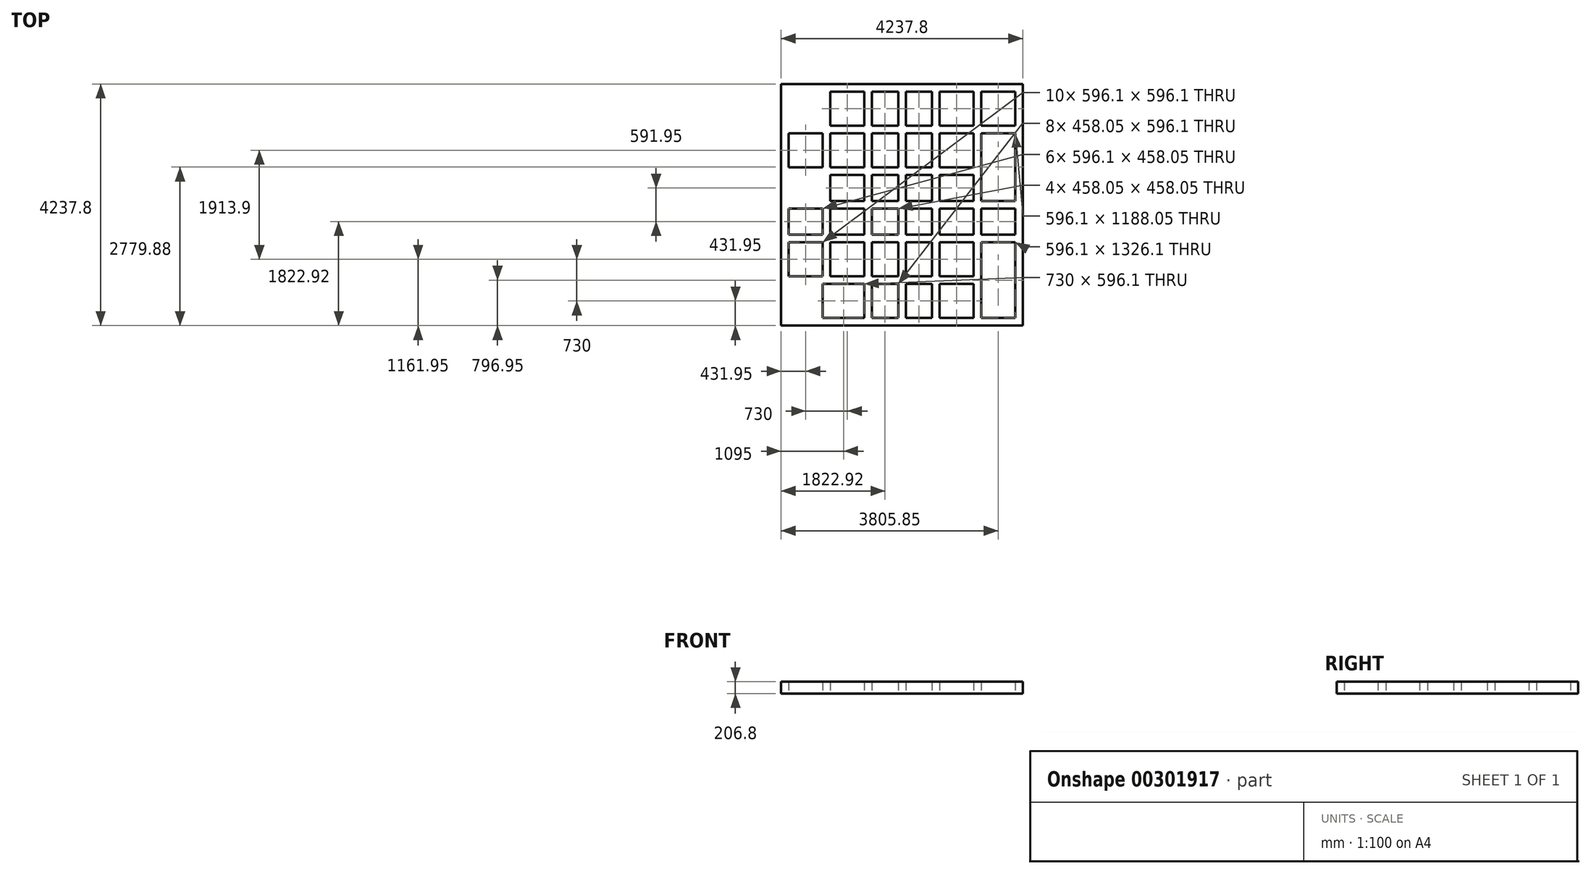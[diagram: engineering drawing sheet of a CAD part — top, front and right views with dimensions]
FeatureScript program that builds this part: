
annotation { "Feature Type Name" : "Feature", "Feature Type Description" : "" }
export const myFeature = defineFeature(function(context is Context, id is Id, definition is map)
    precondition{}
    {
        {
            var Q0;
            Q0=qCreatedBy(makeId("Top.planeOp"),FACE);
            var sketch = newSketch(context, id + "F0", { "sketchPlane" : qUnion([Q0])});
            skCircle(sketch, "E0", {"center": v(0, 0) * mm, "radius": 1985 * mm});
            skLineSegment(sketch, "E1.bottom", {"start": v(-2118.9, 2118.9) * mm, "end": v(2118.9, 2118.9) * mm});
            skLineSegment(sketch, "E1.top", {"start": v(-2118.9, -2118.9) * mm, "end": v(2118.9, -2118.9) * mm});
            skLineSegment(sketch, "E1.left", {"start": v(-2118.9, 2118.9) * mm, "end": v(-2118.9, -2118.9) * mm});
            skLineSegment(sketch, "E1.right", {"start": v(2118.9, 2118.9) * mm, "end": v(2118.9, -2118.9) * mm});
            skLineSegment(sketch, "E2.bottom", {"start": v(-1985, 1985) * mm, "end": v(1985, 1985) * mm});
            skLineSegment(sketch, "E2.top", {"start": v(-1985, -1985) * mm, "end": v(1985, -1985) * mm});
            skLineSegment(sketch, "E2.left", {"start": v(-1985, 1985) * mm, "end": v(-1985, -1985) * mm});
            skLineSegment(sketch, "E2.right", {"start": v(1985, 1985) * mm, "end": v(1985, -1985) * mm});
            skLineSegment(sketch, "E3", {"start": v(1388.9, -1985) * mm, "end": v(1388.9, 1985) * mm});
            skLineSegment(sketch, "E4", {"start": v(1255, -1985) * mm, "end": v(1255, 1985) * mm});
            skLineSegment(sketch, "E5", {"start": v(-525, 1985) * mm, "end": v(-525, -1985) * mm});
            skLineSegment(sketch, "E6", {"start": v(-658.9, 1985) * mm, "end": v(-658.9, -1985) * mm});
            skLineSegment(sketch, "E7", {"start": v(-1255, 1985) * mm, "end": v(-1255, -1985) * mm});
            skLineSegment(sketch, "E8", {"start": v(-1388.9, 1985) * mm, "end": v(-1388.9, -1985) * mm});
            skLineSegment(sketch, "E9", {"start": v(525, 1985) * mm, "end": v(525, -1985) * mm});
            skLineSegment(sketch, "E10", {"start": v(658.9, 1985) * mm, "end": v(658.9, -1985) * mm});
            skLineSegment(sketch, "E11", {"start": v(-1985, 1388.9) * mm, "end": v(1985, 1388.9) * mm});
            skLineSegment(sketch, "E12", {"start": v(-1985, 1255) * mm, "end": v(1985, 1255) * mm});
            skLineSegment(sketch, "E13", {"start": v(-1985, -1388.9) * mm, "end": v(1985, -1388.9) * mm});
            skLineSegment(sketch, "E14", {"start": v(-1985, -1255) * mm, "end": v(1985, -1255) * mm});
            skLineSegment(sketch, "E15", {"start": v(-1985, 658.9) * mm, "end": v(1985, 658.9) * mm});
            skLineSegment(sketch, "E16", {"start": v(-1985, 525) * mm, "end": v(1985, 525) * mm});
            skLineSegment(sketch, "E17", {"start": v(-1985, -525) * mm, "end": v(1985, -525) * mm});
            skLineSegment(sketch, "E18", {"start": v(-1985, -658.9) * mm, "end": v(1985, -658.9) * mm});
            skLineSegment(sketch, "E19", {"start": v(-66.95, 1985) * mm, "end": v(-66.95, -1985) * mm});
            skPoint(sketch, "E19.endSnap0", {"position": v(0, -1985) * mm});
            skLineSegment(sketch, "E20", {"start": v(66.95, 1985) * mm, "end": v(66.95, -1985) * mm});
            skLineSegment(sketch, "E21", {"start": v(-1985, 66.95) * mm, "end": v(1985, 66.95) * mm});
            skLineSegment(sketch, "E22", {"start": v(-1985, -66.95) * mm, "end": v(1985, -66.95) * mm});
            skSolve(sketch);
        }
        {
            var Q0;
            {var subQ0=sQuery(id+"F0.wireOp",EDGE,"E7");var subQ1=sQuery(id+"F0.wireOp",EDGE,"E0");var subQ2=makeQuery(id+"F0.imprint","INTERSECT",VERTEX,{"disambiguationData":[OD(0.0)],"derivedFrom":[subQ1,subQ0]});Q0=makeQuery(id+"F0.imprint","IMPRINT",FACE,{"disambiguationData":[TD([[makeQuery(id+"F0.imprint","IMPRINT",EDGE,{"disambiguationData":[TD([[subQ2,-1.0]])],"derivedFrom":subQ1}),-1.0]])]});}
            var Q1;
            {var subQ0=sQuery(id+"F0.wireOp",EDGE,"E5");var subQ1=sQuery(id+"F0.wireOp",EDGE,"E0");var subQ2=makeQuery(id+"F0.imprint","INTERSECT",VERTEX,{"disambiguationData":[OD(0.0)],"derivedFrom":[subQ1,subQ0]});Q1=makeQuery(id+"F0.imprint","IMPRINT",FACE,{"disambiguationData":[TD([[makeQuery(id+"F0.imprint","IMPRINT",EDGE,{"disambiguationData":[TD([[subQ2,-1.0]])],"derivedFrom":subQ1}),1.0]])]});}
            var Q2;
            {var subQ0=sQuery(id+"F0.wireOp",EDGE,"E5");var subQ1=sQuery(id+"F0.wireOp",EDGE,"E0");var subQ2=makeQuery(id+"F0.imprint","INTERSECT",VERTEX,{"disambiguationData":[OD(0.0)],"derivedFrom":[subQ1,subQ0]});Q2=makeQuery(id+"F0.imprint","IMPRINT",FACE,{"disambiguationData":[TD([[makeQuery(id+"F0.imprint","IMPRINT",EDGE,{"disambiguationData":[TD([[subQ2,-1.0]])],"derivedFrom":subQ1}),-1.0]])]});}
            var Q3;
            Q3=makeQuery(id+"F0.imprint","IMPRINT",FACE,{"disambiguationData":[TD([[makeQuery(id+"F0.imprint","IMPRINT",EDGE,{"derivedFrom":sQuery(id+"F0.wireOp",EDGE,"E1.bottom")}),-1.0]])]});
            var Q4;
            {var subQ0=sQuery(id+"F0.wireOp",EDGE,"E11");var subQ1=sQuery(id+"F0.wireOp",EDGE,"E0");var subQ2=makeQuery(id+"F0.imprint","INTERSECT",VERTEX,{"disambiguationData":[OD(1.0)],"derivedFrom":[subQ1,subQ0]});Q4=makeQuery(id+"F0.imprint","IMPRINT",FACE,{"disambiguationData":[TD([[makeQuery(id+"F0.imprint","IMPRINT",EDGE,{"disambiguationData":[TD([[subQ2,-1.0]])],"derivedFrom":subQ1}),-1.0]])]});}
            var Q5;
            {var subQ0=sQuery(id+"F0.wireOp",EDGE,"E11");var subQ1=sQuery(id+"F0.wireOp",EDGE,"E0");var subQ2=makeQuery(id+"F0.imprint","INTERSECT",VERTEX,{"disambiguationData":[OD(1.0)],"derivedFrom":[subQ1,subQ0]});Q5=makeQuery(id+"F0.imprint","IMPRINT",FACE,{"disambiguationData":[TD([[makeQuery(id+"F0.imprint","IMPRINT",EDGE,{"disambiguationData":[TD([[subQ2,-1.0]])],"derivedFrom":subQ1}),1.0]])]});}
            var Q6;
            {var subQ0=sQuery(id+"F0.wireOp",EDGE,"E11");var subQ1=sQuery(id+"F0.wireOp",EDGE,"E7");var subQ2=makeQuery(id+"F0.imprint","INTERSECT",VERTEX,{"derivedFrom":[subQ1,subQ0]});Q6=makeQuery(id+"F0.imprint","IMPRINT",FACE,{"disambiguationData":[TD([[makeQuery(id+"F0.imprint","IMPRINT",EDGE,{"disambiguationData":[TD([[subQ2,-1.0]])],"derivedFrom":subQ1}),-1.0]])]});}
            var Q7;
            {var subQ0=sQuery(id+"F0.wireOp",EDGE,"E11");var subQ1=sQuery(id+"F0.wireOp",EDGE,"E6");var subQ2=makeQuery(id+"F0.imprint","INTERSECT",VERTEX,{"derivedFrom":[subQ1,subQ0]});Q7=makeQuery(id+"F0.imprint","IMPRINT",FACE,{"disambiguationData":[TD([[makeQuery(id+"F0.imprint","IMPRINT",EDGE,{"disambiguationData":[TD([[subQ2,-1.0]])],"derivedFrom":subQ1}),-1.0]])]});}
            var Q8;
            {var subQ0=sQuery(id+"F0.wireOp",EDGE,"E7");var subQ1=sQuery(id+"F0.wireOp",EDGE,"E0");var subQ2=makeQuery(id+"F0.imprint","INTERSECT",VERTEX,{"disambiguationData":[OD(0.0)],"derivedFrom":[subQ1,subQ0]});Q8=makeQuery(id+"F0.imprint","IMPRINT",FACE,{"disambiguationData":[TD([[makeQuery(id+"F0.imprint","IMPRINT",EDGE,{"disambiguationData":[TD([[subQ2,-1.0]])],"derivedFrom":subQ1}),1.0]])]});}
            var Q9;
            {var subQ0=sQuery(id+"F0.wireOp",EDGE,"E12");var subQ1=sQuery(id+"F0.wireOp",EDGE,"E7");var subQ2=makeQuery(id+"F0.imprint","INTERSECT",VERTEX,{"derivedFrom":[subQ1,subQ0]});Q9=makeQuery(id+"F0.imprint","IMPRINT",FACE,{"disambiguationData":[TD([[makeQuery(id+"F0.imprint","IMPRINT",EDGE,{"disambiguationData":[TD([[subQ2,-1.0]])],"derivedFrom":subQ1}),-1.0]])]});}
            var Q10;
            {var subQ0=sQuery(id+"F0.wireOp",EDGE,"E16");var subQ1=sQuery(id+"F0.wireOp",EDGE,"E7");var subQ2=makeQuery(id+"F0.imprint","INTERSECT",VERTEX,{"derivedFrom":[subQ1,subQ0]});Q10=makeQuery(id+"F0.imprint","IMPRINT",FACE,{"disambiguationData":[TD([[makeQuery(id+"F0.imprint","IMPRINT",EDGE,{"disambiguationData":[TD([[subQ2,-1.0]])],"derivedFrom":subQ1}),-1.0]])]});}
            var Q11;
            {var subQ0=sQuery(id+"F0.wireOp",EDGE,"E15");var subQ1=sQuery(id+"F0.wireOp",EDGE,"E7");var subQ2=makeQuery(id+"F0.imprint","INTERSECT",VERTEX,{"derivedFrom":[subQ1,subQ0]});Q11=makeQuery(id+"F0.imprint","IMPRINT",FACE,{"disambiguationData":[TD([[makeQuery(id+"F0.imprint","IMPRINT",EDGE,{"disambiguationData":[TD([[subQ2,-1.0]])],"derivedFrom":subQ1}),-1.0]])]});}
            var Q12;
            {var subQ0=sQuery(id+"F0.wireOp",EDGE,"E15");var subQ1=sQuery(id+"F0.wireOp",EDGE,"E0");var subQ2=makeQuery(id+"F0.imprint","INTERSECT",VERTEX,{"disambiguationData":[OD(1.0)],"derivedFrom":[subQ1,subQ0]});Q12=makeQuery(id+"F0.imprint","IMPRINT",FACE,{"disambiguationData":[TD([[makeQuery(id+"F0.imprint","IMPRINT",EDGE,{"disambiguationData":[TD([[subQ2,-1.0]])],"derivedFrom":subQ1}),1.0]])]});}
            var Q13;
            {var subQ0=sQuery(id+"F0.wireOp",EDGE,"E15");var subQ1=sQuery(id+"F0.wireOp",EDGE,"E0");var subQ2=makeQuery(id+"F0.imprint","INTERSECT",VERTEX,{"disambiguationData":[OD(1.0)],"derivedFrom":[subQ1,subQ0]});Q13=makeQuery(id+"F0.imprint","IMPRINT",FACE,{"disambiguationData":[TD([[makeQuery(id+"F0.imprint","IMPRINT",EDGE,{"disambiguationData":[TD([[subQ2,-1.0]])],"derivedFrom":subQ1}),-1.0]])]});}
            var Q14;
            {var subQ0=sQuery(id+"F0.wireOp",EDGE,"E21");var subQ1=sQuery(id+"F0.wireOp",EDGE,"E7");var subQ2=makeQuery(id+"F0.imprint","INTERSECT",VERTEX,{"derivedFrom":[subQ1,subQ0]});Q14=makeQuery(id+"F0.imprint","IMPRINT",FACE,{"disambiguationData":[TD([[makeQuery(id+"F0.imprint","IMPRINT",EDGE,{"disambiguationData":[TD([[subQ2,-1.0]])],"derivedFrom":subQ1}),-1.0]])]});}
            var Q15;
            {var subQ0=sQuery(id+"F0.wireOp",EDGE,"E2.left");var subQ1=sQuery(id+"F0.wireOp",EDGE,"E0");var subQ2=makeQuery(id+"F0.imprint","INTERSECT",VERTEX,{"derivedFrom":[subQ1,subQ0]});Q15=makeQuery(id+"F0.imprint","IMPRINT",FACE,{"disambiguationData":[TD([[makeQuery(id+"F0.imprint","IMPRINT",EDGE,{"disambiguationData":[TD([[subQ2,-1.0]])],"derivedFrom":subQ1}),-1.0]])]});}
            var Q16;
            {var subQ0=sQuery(id+"F0.wireOp",EDGE,"E21");var subQ5=sQuery(id+"F0.wireOp",EDGE,"E0");var subQ8=makeQuery(id+"F0.imprint","INTERSECT",VERTEX,{"disambiguationData":[OD(1.0)],"derivedFrom":[subQ5,subQ0]});Q16=makeQuery(id+"F0.imprint","IMPRINT",FACE,{"disambiguationData":[TD([[makeQuery(id+"F0.imprint","IMPRINT",EDGE,{"disambiguationData":[TD([[subQ8,-1.0]])],"derivedFrom":subQ5}),1.0]])]});}
            var Q17;
            {var subQ0=sQuery(id+"F0.wireOp",EDGE,"E21");var subQ1=sQuery(id+"F0.wireOp",EDGE,"E0");var subQ2=makeQuery(id+"F0.imprint","INTERSECT",VERTEX,{"disambiguationData":[OD(1.0)],"derivedFrom":[subQ1,subQ0]});Q17=makeQuery(id+"F0.imprint","IMPRINT",FACE,{"disambiguationData":[TD([[makeQuery(id+"F0.imprint","IMPRINT",EDGE,{"disambiguationData":[TD([[subQ2,-1.0]])],"derivedFrom":subQ1}),-1.0]])]});}
            var Q18;
            {var subQ0=sQuery(id+"F0.wireOp",EDGE,"E22");var subQ1=sQuery(id+"F0.wireOp",EDGE,"E7");var subQ2=makeQuery(id+"F0.imprint","INTERSECT",VERTEX,{"derivedFrom":[subQ1,subQ0]});Q18=makeQuery(id+"F0.imprint","IMPRINT",FACE,{"disambiguationData":[TD([[makeQuery(id+"F0.imprint","IMPRINT",EDGE,{"disambiguationData":[TD([[subQ2,-1.0]])],"derivedFrom":subQ1}),-1.0]])]});}
            var Q19;
            {var subQ0=sQuery(id+"F0.wireOp",EDGE,"E17");var subQ1=sQuery(id+"F0.wireOp",EDGE,"E0");var subQ2=makeQuery(id+"F0.imprint","INTERSECT",VERTEX,{"disambiguationData":[OD(0.0)],"derivedFrom":[subQ1,subQ0]});Q19=makeQuery(id+"F0.imprint","IMPRINT",FACE,{"disambiguationData":[TD([[makeQuery(id+"F0.imprint","IMPRINT",EDGE,{"disambiguationData":[TD([[subQ2,-1.0]])],"derivedFrom":subQ1}),1.0]])]});}
            var Q20;
            {var subQ0=sQuery(id+"F0.wireOp",EDGE,"E17");var subQ1=sQuery(id+"F0.wireOp",EDGE,"E7");var subQ2=makeQuery(id+"F0.imprint","INTERSECT",VERTEX,{"derivedFrom":[subQ1,subQ0]});Q20=makeQuery(id+"F0.imprint","IMPRINT",FACE,{"disambiguationData":[TD([[makeQuery(id+"F0.imprint","IMPRINT",EDGE,{"disambiguationData":[TD([[subQ2,-1.0]])],"derivedFrom":subQ1}),-1.0]])]});}
            var Q21;
            {var subQ0=sQuery(id+"F0.wireOp",EDGE,"E17");var subQ1=sQuery(id+"F0.wireOp",EDGE,"E6");var subQ2=makeQuery(id+"F0.imprint","INTERSECT",VERTEX,{"derivedFrom":[subQ1,subQ0]});Q21=makeQuery(id+"F0.imprint","IMPRINT",FACE,{"disambiguationData":[TD([[makeQuery(id+"F0.imprint","IMPRINT",EDGE,{"disambiguationData":[TD([[subQ2,-1.0]])],"derivedFrom":subQ1}),-1.0]])]});}
            var Q22;
            {var subQ0=sQuery(id+"F0.wireOp",EDGE,"E18");var subQ1=sQuery(id+"F0.wireOp",EDGE,"E7");var subQ2=makeQuery(id+"F0.imprint","INTERSECT",VERTEX,{"derivedFrom":[subQ1,subQ0]});Q22=makeQuery(id+"F0.imprint","IMPRINT",FACE,{"disambiguationData":[TD([[makeQuery(id+"F0.imprint","IMPRINT",EDGE,{"disambiguationData":[TD([[subQ2,-1.0]])],"derivedFrom":subQ1}),-1.0]])]});}
            var Q23;
            {var subQ0=sQuery(id+"F0.wireOp",EDGE,"E21");var subQ1=sQuery(id+"F0.wireOp",EDGE,"E6");var subQ2=makeQuery(id+"F0.imprint","INTERSECT",VERTEX,{"derivedFrom":[subQ1,subQ0]});Q23=makeQuery(id+"F0.imprint","IMPRINT",FACE,{"disambiguationData":[TD([[makeQuery(id+"F0.imprint","IMPRINT",EDGE,{"disambiguationData":[TD([[subQ2,-1.0]])],"derivedFrom":subQ1}),-1.0]])]});}
            var Q24;
            {var subQ0=sQuery(id+"F0.wireOp",EDGE,"E21");var subQ1=sQuery(id+"F0.wireOp",EDGE,"E5");var subQ2=makeQuery(id+"F0.imprint","INTERSECT",VERTEX,{"derivedFrom":[subQ1,subQ0]});Q24=makeQuery(id+"F0.imprint","IMPRINT",FACE,{"disambiguationData":[TD([[makeQuery(id+"F0.imprint","IMPRINT",EDGE,{"disambiguationData":[TD([[subQ2,-1.0]])],"derivedFrom":subQ1}),-1.0]])]});}
            var Q25;
            {var subQ0=sQuery(id+"F0.wireOp",EDGE,"E22");var subQ1=sQuery(id+"F0.wireOp",EDGE,"E5");var subQ2=makeQuery(id+"F0.imprint","INTERSECT",VERTEX,{"derivedFrom":[subQ1,subQ0]});Q25=makeQuery(id+"F0.imprint","IMPRINT",FACE,{"disambiguationData":[TD([[makeQuery(id+"F0.imprint","IMPRINT",EDGE,{"disambiguationData":[TD([[subQ2,-1.0]])],"derivedFrom":subQ1}),-1.0]])]});}
            var Q26;
            {var subQ0=sQuery(id+"F0.wireOp",EDGE,"E18");var subQ1=sQuery(id+"F0.wireOp",EDGE,"E5");var subQ2=makeQuery(id+"F0.imprint","INTERSECT",VERTEX,{"derivedFrom":[subQ1,subQ0]});Q26=makeQuery(id+"F0.imprint","IMPRINT",FACE,{"disambiguationData":[TD([[makeQuery(id+"F0.imprint","IMPRINT",EDGE,{"disambiguationData":[TD([[subQ2,-1.0]])],"derivedFrom":subQ1}),-1.0]])]});}
            var Q27;
            {var subQ0=sQuery(id+"F0.wireOp",EDGE,"E17");var subQ1=sQuery(id+"F0.wireOp",EDGE,"E5");var subQ2=makeQuery(id+"F0.imprint","INTERSECT",VERTEX,{"derivedFrom":[subQ1,subQ0]});Q27=makeQuery(id+"F0.imprint","IMPRINT",FACE,{"disambiguationData":[TD([[makeQuery(id+"F0.imprint","IMPRINT",EDGE,{"disambiguationData":[TD([[subQ2,-1.0]])],"derivedFrom":subQ1}),-1.0]])]});}
            var Q28;
            {var subQ0=sQuery(id+"F0.wireOp",EDGE,"E17");var subQ1=sQuery(id+"F0.wireOp",EDGE,"E5");var subQ2=makeQuery(id+"F0.imprint","INTERSECT",VERTEX,{"derivedFrom":[subQ1,subQ0]});Q28=makeQuery(id+"F0.imprint","IMPRINT",FACE,{"disambiguationData":[TD([[makeQuery(id+"F0.imprint","IMPRINT",EDGE,{"disambiguationData":[TD([[subQ2,-1.0]])],"derivedFrom":subQ1}),1.0]])]});}
            var Q29;
            {var subQ0=sQuery(id+"F0.wireOp",EDGE,"E21");var subQ1=sQuery(id+"F0.wireOp",EDGE,"E5");var subQ2=makeQuery(id+"F0.imprint","INTERSECT",VERTEX,{"derivedFrom":[subQ1,subQ0]});Q29=makeQuery(id+"F0.imprint","IMPRINT",FACE,{"disambiguationData":[TD([[makeQuery(id+"F0.imprint","IMPRINT",EDGE,{"disambiguationData":[TD([[subQ2,-1.0]])],"derivedFrom":subQ1}),1.0]])]});}
            var Q30;
            {var subQ0=sQuery(id+"F0.wireOp",EDGE,"E16");var subQ1=sQuery(id+"F0.wireOp",EDGE,"E5");var subQ2=makeQuery(id+"F0.imprint","INTERSECT",VERTEX,{"derivedFrom":[subQ1,subQ0]});Q30=makeQuery(id+"F0.imprint","IMPRINT",FACE,{"disambiguationData":[TD([[makeQuery(id+"F0.imprint","IMPRINT",EDGE,{"disambiguationData":[TD([[subQ2,-1.0]])],"derivedFrom":subQ1}),-1.0]])]});}
            var Q31;
            {var subQ0=sQuery(id+"F0.wireOp",EDGE,"E15");var subQ1=sQuery(id+"F0.wireOp",EDGE,"E5");var subQ2=makeQuery(id+"F0.imprint","INTERSECT",VERTEX,{"derivedFrom":[subQ1,subQ0]});Q31=makeQuery(id+"F0.imprint","IMPRINT",FACE,{"disambiguationData":[TD([[makeQuery(id+"F0.imprint","IMPRINT",EDGE,{"disambiguationData":[TD([[subQ2,-1.0]])],"derivedFrom":subQ1}),1.0]])]});}
            var Q32;
            {var subQ0=sQuery(id+"F0.wireOp",EDGE,"E15");var subQ1=sQuery(id+"F0.wireOp",EDGE,"E6");var subQ2=makeQuery(id+"F0.imprint","INTERSECT",VERTEX,{"derivedFrom":[subQ1,subQ0]});Q32=makeQuery(id+"F0.imprint","IMPRINT",FACE,{"disambiguationData":[TD([[makeQuery(id+"F0.imprint","IMPRINT",EDGE,{"disambiguationData":[TD([[subQ2,-1.0]])],"derivedFrom":subQ1}),-1.0]])]});}
            var Q33;
            {var subQ0=sQuery(id+"F0.wireOp",EDGE,"E15");var subQ1=sQuery(id+"F0.wireOp",EDGE,"E5");var subQ2=makeQuery(id+"F0.imprint","INTERSECT",VERTEX,{"derivedFrom":[subQ1,subQ0]});Q33=makeQuery(id+"F0.imprint","IMPRINT",FACE,{"disambiguationData":[TD([[makeQuery(id+"F0.imprint","IMPRINT",EDGE,{"disambiguationData":[TD([[subQ2,-1.0]])],"derivedFrom":subQ1}),-1.0]])]});}
            var Q34;
            {var subQ0=sQuery(id+"F0.wireOp",EDGE,"E17");var subQ1=sQuery(id+"F0.wireOp",EDGE,"E0");var subQ2=makeQuery(id+"F0.imprint","INTERSECT",VERTEX,{"disambiguationData":[OD(0.0)],"derivedFrom":[subQ1,subQ0]});Q34=makeQuery(id+"F0.imprint","IMPRINT",FACE,{"disambiguationData":[TD([[makeQuery(id+"F0.imprint","IMPRINT",EDGE,{"disambiguationData":[TD([[subQ2,-1.0]])],"derivedFrom":subQ1}),-1.0]])]});}
            var Q35;
            {var subQ0=sQuery(id+"F0.wireOp",EDGE,"E14");var subQ1=sQuery(id+"F0.wireOp",EDGE,"E0");var subQ2=makeQuery(id+"F0.imprint","INTERSECT",VERTEX,{"disambiguationData":[OD(0.0)],"derivedFrom":[subQ1,subQ0]});Q35=makeQuery(id+"F0.imprint","IMPRINT",FACE,{"disambiguationData":[TD([[makeQuery(id+"F0.imprint","IMPRINT",EDGE,{"disambiguationData":[TD([[subQ2,-1.0]])],"derivedFrom":subQ1}),-1.0]])]});}
            var Q36;
            {var subQ0=sQuery(id+"F0.wireOp",EDGE,"E14");var subQ1=sQuery(id+"F0.wireOp",EDGE,"E0");var subQ2=makeQuery(id+"F0.imprint","INTERSECT",VERTEX,{"disambiguationData":[OD(0.0)],"derivedFrom":[subQ1,subQ0]});Q36=makeQuery(id+"F0.imprint","IMPRINT",FACE,{"disambiguationData":[TD([[makeQuery(id+"F0.imprint","IMPRINT",EDGE,{"disambiguationData":[TD([[subQ2,-1.0]])],"derivedFrom":subQ1}),1.0]])]});}
            var Q37;
            {var subQ0=sQuery(id+"F0.wireOp",EDGE,"E14");var subQ1=sQuery(id+"F0.wireOp",EDGE,"E7");var subQ2=makeQuery(id+"F0.imprint","INTERSECT",VERTEX,{"derivedFrom":[subQ1,subQ0]});Q37=makeQuery(id+"F0.imprint","IMPRINT",FACE,{"disambiguationData":[TD([[makeQuery(id+"F0.imprint","IMPRINT",EDGE,{"disambiguationData":[TD([[subQ2,-1.0]])],"derivedFrom":subQ1}),-1.0]])]});}
            var Q38;
            {var subQ0=sQuery(id+"F0.wireOp",EDGE,"E8");var subQ1=sQuery(id+"F0.wireOp",EDGE,"E0");var subQ2=makeQuery(id+"F0.imprint","INTERSECT",VERTEX,{"disambiguationData":[OD(1.0)],"derivedFrom":[subQ1,subQ0]});Q38=makeQuery(id+"F0.imprint","IMPRINT",FACE,{"disambiguationData":[TD([[makeQuery(id+"F0.imprint","IMPRINT",EDGE,{"disambiguationData":[TD([[subQ2,-1.0]])],"derivedFrom":subQ1}),-1.0]])]});}
            var Q39;
            {var subQ0=sQuery(id+"F0.wireOp",EDGE,"E8");var subQ1=sQuery(id+"F0.wireOp",EDGE,"E0");var subQ2=makeQuery(id+"F0.imprint","INTERSECT",VERTEX,{"disambiguationData":[OD(1.0)],"derivedFrom":[subQ1,subQ0]});Q39=makeQuery(id+"F0.imprint","IMPRINT",FACE,{"disambiguationData":[TD([[makeQuery(id+"F0.imprint","IMPRINT",EDGE,{"disambiguationData":[TD([[subQ2,-1.0]])],"derivedFrom":subQ1}),1.0]])]});}
            var Q40;
            {var subQ0=sQuery(id+"F0.wireOp",EDGE,"E6");var subQ1=sQuery(id+"F0.wireOp",EDGE,"E0");var subQ2=makeQuery(id+"F0.imprint","INTERSECT",VERTEX,{"disambiguationData":[OD(1.0)],"derivedFrom":[subQ1,subQ0]});Q40=makeQuery(id+"F0.imprint","IMPRINT",FACE,{"disambiguationData":[TD([[makeQuery(id+"F0.imprint","IMPRINT",EDGE,{"disambiguationData":[TD([[subQ2,-1.0]])],"derivedFrom":subQ1}),1.0]])]});}
            var Q41;
            {var subQ0=sQuery(id+"F0.wireOp",EDGE,"E14");var subQ1=sQuery(id+"F0.wireOp",EDGE,"E5");var subQ2=makeQuery(id+"F0.imprint","INTERSECT",VERTEX,{"derivedFrom":[subQ1,subQ0]});Q41=makeQuery(id+"F0.imprint","IMPRINT",FACE,{"disambiguationData":[TD([[makeQuery(id+"F0.imprint","IMPRINT",EDGE,{"disambiguationData":[TD([[subQ2,-1.0]])],"derivedFrom":subQ1}),-1.0]])]});}
            var Q42;
            {var subQ0=sQuery(id+"F0.wireOp",EDGE,"E14");var subQ1=sQuery(id+"F0.wireOp",EDGE,"E6");var subQ2=makeQuery(id+"F0.imprint","INTERSECT",VERTEX,{"derivedFrom":[subQ1,subQ0]});Q42=makeQuery(id+"F0.imprint","IMPRINT",FACE,{"disambiguationData":[TD([[makeQuery(id+"F0.imprint","IMPRINT",EDGE,{"disambiguationData":[TD([[subQ2,-1.0]])],"derivedFrom":subQ1}),-1.0]])]});}
            var Q43;
            {var subQ0=sQuery(id+"F0.wireOp",EDGE,"E14");var subQ1=sQuery(id+"F0.wireOp",EDGE,"E5");var subQ2=makeQuery(id+"F0.imprint","INTERSECT",VERTEX,{"derivedFrom":[subQ1,subQ0]});Q43=makeQuery(id+"F0.imprint","IMPRINT",FACE,{"disambiguationData":[TD([[makeQuery(id+"F0.imprint","IMPRINT",EDGE,{"disambiguationData":[TD([[subQ2,-1.0]])],"derivedFrom":subQ1}),1.0]])]});}
            var Q44;
            {var subQ0=sQuery(id+"F0.wireOp",EDGE,"E19");var subQ1=sQuery(id+"F0.wireOp",EDGE,"E13");var subQ2=makeQuery(id+"F0.imprint","INTERSECT",VERTEX,{"derivedFrom":[subQ1,subQ0]});Q44=makeQuery(id+"F0.imprint","IMPRINT",FACE,{"disambiguationData":[TD([[makeQuery(id+"F0.imprint","IMPRINT",EDGE,{"disambiguationData":[TD([[subQ2,-1.0]])],"derivedFrom":subQ1}),1.0]])]});}
            var Q45;
            {var subQ0=sQuery(id+"F0.wireOp",EDGE,"E19");var subQ1=sQuery(id+"F0.wireOp",EDGE,"E14");var subQ2=makeQuery(id+"F0.imprint","INTERSECT",VERTEX,{"derivedFrom":[subQ1,subQ0]});Q45=makeQuery(id+"F0.imprint","IMPRINT",FACE,{"disambiguationData":[TD([[makeQuery(id+"F0.imprint","IMPRINT",EDGE,{"disambiguationData":[TD([[subQ2,-1.0]])],"derivedFrom":subQ1}),1.0]])]});}
            var Q46;
            {var subQ0=sQuery(id+"F0.wireOp",EDGE,"E19");var subQ1=sQuery(id+"F0.wireOp",EDGE,"E17");var subQ2=makeQuery(id+"F0.imprint","INTERSECT",VERTEX,{"derivedFrom":[subQ1,subQ0]});Q46=makeQuery(id+"F0.imprint","IMPRINT",FACE,{"disambiguationData":[TD([[makeQuery(id+"F0.imprint","IMPRINT",EDGE,{"disambiguationData":[TD([[subQ2,-1.0]])],"derivedFrom":subQ1}),-1.0]])]});}
            var Q47;
            {var subQ0=sQuery(id+"F0.wireOp",EDGE,"E19");var subQ1=sQuery(id+"F0.wireOp",EDGE,"E17");var subQ2=makeQuery(id+"F0.imprint","INTERSECT",VERTEX,{"derivedFrom":[subQ1,subQ0]});Q47=makeQuery(id+"F0.imprint","IMPRINT",FACE,{"disambiguationData":[TD([[makeQuery(id+"F0.imprint","IMPRINT",EDGE,{"disambiguationData":[TD([[subQ2,-1.0]])],"derivedFrom":subQ1}),1.0]])]});}
            var Q48;
            {var subQ0=sQuery(id+"F0.wireOp",EDGE,"E21");var subQ1=sQuery(id+"F0.wireOp",EDGE,"E19");var subQ2=makeQuery(id+"F0.imprint","INTERSECT",VERTEX,{"derivedFrom":[subQ1,subQ0]});Q48=makeQuery(id+"F0.imprint","IMPRINT",FACE,{"disambiguationData":[TD([[makeQuery(id+"F0.imprint","IMPRINT",EDGE,{"disambiguationData":[TD([[subQ2,-1.0]])],"derivedFrom":subQ1}),1.0]])]});}
            var Q49;
            {var subQ0=sQuery(id+"F0.wireOp",EDGE,"E19");var subQ1=sQuery(id+"F0.wireOp",EDGE,"E16");var subQ2=makeQuery(id+"F0.imprint","INTERSECT",VERTEX,{"derivedFrom":[subQ1,subQ0]});Q49=makeQuery(id+"F0.imprint","IMPRINT",FACE,{"disambiguationData":[TD([[makeQuery(id+"F0.imprint","IMPRINT",EDGE,{"disambiguationData":[TD([[subQ2,-1.0]])],"derivedFrom":subQ1}),-1.0]])]});}
            var Q50;
            {var subQ0=sQuery(id+"F0.wireOp",EDGE,"E19");var subQ1=sQuery(id+"F0.wireOp",EDGE,"E15");var subQ2=makeQuery(id+"F0.imprint","INTERSECT",VERTEX,{"derivedFrom":[subQ1,subQ0]});Q50=makeQuery(id+"F0.imprint","IMPRINT",FACE,{"disambiguationData":[TD([[makeQuery(id+"F0.imprint","IMPRINT",EDGE,{"disambiguationData":[TD([[subQ2,-1.0]])],"derivedFrom":subQ1}),-1.0]])]});}
            var Q51;
            {var subQ0=sQuery(id+"F0.wireOp",EDGE,"E12");var subQ1=sQuery(id+"F0.wireOp",EDGE,"E5");var subQ2=makeQuery(id+"F0.imprint","INTERSECT",VERTEX,{"derivedFrom":[subQ1,subQ0]});Q51=makeQuery(id+"F0.imprint","IMPRINT",FACE,{"disambiguationData":[TD([[makeQuery(id+"F0.imprint","IMPRINT",EDGE,{"disambiguationData":[TD([[subQ2,-1.0]])],"derivedFrom":subQ1}),-1.0]])]});}
            var Q52;
            {var subQ0=sQuery(id+"F0.wireOp",EDGE,"E11");var subQ1=sQuery(id+"F0.wireOp",EDGE,"E5");var subQ2=makeQuery(id+"F0.imprint","INTERSECT",VERTEX,{"derivedFrom":[subQ1,subQ0]});Q52=makeQuery(id+"F0.imprint","IMPRINT",FACE,{"disambiguationData":[TD([[makeQuery(id+"F0.imprint","IMPRINT",EDGE,{"disambiguationData":[TD([[subQ2,-1.0]])],"derivedFrom":subQ1}),-1.0]])]});}
            var Q53;
            {var subQ0=sQuery(id+"F0.wireOp",EDGE,"E11");var subQ1=sQuery(id+"F0.wireOp",EDGE,"E5");var subQ2=makeQuery(id+"F0.imprint","INTERSECT",VERTEX,{"derivedFrom":[subQ1,subQ0]});Q53=makeQuery(id+"F0.imprint","IMPRINT",FACE,{"disambiguationData":[TD([[makeQuery(id+"F0.imprint","IMPRINT",EDGE,{"disambiguationData":[TD([[subQ2,-1.0]])],"derivedFrom":subQ1}),1.0]])]});}
            var Q54;
            {var subQ0=sQuery(id+"F0.wireOp",EDGE,"E19");var subQ1=sQuery(id+"F0.wireOp",EDGE,"E11");var subQ2=makeQuery(id+"F0.imprint","INTERSECT",VERTEX,{"derivedFrom":[subQ1,subQ0]});Q54=makeQuery(id+"F0.imprint","IMPRINT",FACE,{"disambiguationData":[TD([[makeQuery(id+"F0.imprint","IMPRINT",EDGE,{"disambiguationData":[TD([[subQ2,-1.0]])],"derivedFrom":subQ1}),-1.0]])]});}
            var Q55;
            {var subQ3=sQuery(id+"F0.wireOp",EDGE,"E20");var subQ5=sQuery(id+"F0.wireOp",EDGE,"E0");var subQ8=makeQuery(id+"F0.imprint","INTERSECT",VERTEX,{"disambiguationData":[OD(0.0)],"derivedFrom":[subQ5,subQ3]});Q55=makeQuery(id+"F0.imprint","IMPRINT",FACE,{"disambiguationData":[TD([[makeQuery(id+"F0.imprint","IMPRINT",EDGE,{"disambiguationData":[TD([[subQ8,-1.0]])],"derivedFrom":subQ5}),1.0]])]});}
            var Q56;
            {var subQ0=sQuery(id+"F0.wireOp",EDGE,"E2.bottom");var subQ1=sQuery(id+"F0.wireOp",EDGE,"E0");var subQ2=makeQuery(id+"F0.imprint","INTERSECT",VERTEX,{"derivedFrom":[subQ1,subQ0]});Q56=makeQuery(id+"F0.imprint","IMPRINT",FACE,{"disambiguationData":[TD([[makeQuery(id+"F0.imprint","IMPRINT",EDGE,{"disambiguationData":[TD([[subQ2,-1.0]])],"derivedFrom":subQ1}),-1.0]])]});}
            var Q57;
            {var subQ0=sQuery(id+"F0.wireOp",EDGE,"E20");var subQ1=sQuery(id+"F0.wireOp",EDGE,"E0");var subQ2=makeQuery(id+"F0.imprint","INTERSECT",VERTEX,{"disambiguationData":[OD(0.0)],"derivedFrom":[subQ1,subQ0]});Q57=makeQuery(id+"F0.imprint","IMPRINT",FACE,{"disambiguationData":[TD([[makeQuery(id+"F0.imprint","IMPRINT",EDGE,{"disambiguationData":[TD([[subQ2,-1.0]])],"derivedFrom":subQ1}),-1.0]])]});}
            var Q58;
            {var subQ0=sQuery(id+"F0.wireOp",EDGE,"E10");var subQ1=sQuery(id+"F0.wireOp",EDGE,"E0");var subQ2=makeQuery(id+"F0.imprint","INTERSECT",VERTEX,{"disambiguationData":[OD(0.0)],"derivedFrom":[subQ1,subQ0]});Q58=makeQuery(id+"F0.imprint","IMPRINT",FACE,{"disambiguationData":[TD([[makeQuery(id+"F0.imprint","IMPRINT",EDGE,{"disambiguationData":[TD([[subQ2,-1.0]])],"derivedFrom":subQ1}),-1.0]])]});}
            var Q59;
            {var subQ0=sQuery(id+"F0.wireOp",EDGE,"E10");var subQ1=sQuery(id+"F0.wireOp",EDGE,"E0");var subQ2=makeQuery(id+"F0.imprint","INTERSECT",VERTEX,{"disambiguationData":[OD(0.0)],"derivedFrom":[subQ1,subQ0]});Q59=makeQuery(id+"F0.imprint","IMPRINT",FACE,{"disambiguationData":[TD([[makeQuery(id+"F0.imprint","IMPRINT",EDGE,{"disambiguationData":[TD([[subQ2,-1.0]])],"derivedFrom":subQ1}),1.0]])]});}
            var Q60;
            {var subQ0=sQuery(id+"F0.wireOp",EDGE,"E11");var subQ1=sQuery(id+"F0.wireOp",EDGE,"E9");var subQ2=makeQuery(id+"F0.imprint","INTERSECT",VERTEX,{"derivedFrom":[subQ1,subQ0]});Q60=makeQuery(id+"F0.imprint","IMPRINT",FACE,{"disambiguationData":[TD([[makeQuery(id+"F0.imprint","IMPRINT",EDGE,{"disambiguationData":[TD([[subQ2,-1.0]])],"derivedFrom":subQ1}),-1.0]])]});}
            var Q61;
            {var subQ0=sQuery(id+"F0.wireOp",EDGE,"E11");var subQ1=sQuery(id+"F0.wireOp",EDGE,"E9");var subQ2=makeQuery(id+"F0.imprint","INTERSECT",VERTEX,{"derivedFrom":[subQ1,subQ0]});Q61=makeQuery(id+"F0.imprint","IMPRINT",FACE,{"disambiguationData":[TD([[makeQuery(id+"F0.imprint","IMPRINT",EDGE,{"disambiguationData":[TD([[subQ2,-1.0]])],"derivedFrom":subQ1}),1.0]])]});}
            var Q62;
            {var subQ0=sQuery(id+"F0.wireOp",EDGE,"E19");var subQ1=sQuery(id+"F0.wireOp",EDGE,"E12");var subQ2=makeQuery(id+"F0.imprint","INTERSECT",VERTEX,{"derivedFrom":[subQ1,subQ0]});Q62=makeQuery(id+"F0.imprint","IMPRINT",FACE,{"disambiguationData":[TD([[makeQuery(id+"F0.imprint","IMPRINT",EDGE,{"disambiguationData":[TD([[subQ2,-1.0]])],"derivedFrom":subQ1}),-1.0]])]});}
            var Q63;
            {var subQ0=sQuery(id+"F0.wireOp",EDGE,"E15");var subQ1=sQuery(id+"F0.wireOp",EDGE,"E9");var subQ2=makeQuery(id+"F0.imprint","INTERSECT",VERTEX,{"derivedFrom":[subQ1,subQ0]});Q63=makeQuery(id+"F0.imprint","IMPRINT",FACE,{"disambiguationData":[TD([[makeQuery(id+"F0.imprint","IMPRINT",EDGE,{"disambiguationData":[TD([[subQ2,-1.0]])],"derivedFrom":subQ1}),-1.0]])]});}
            var Q64;
            {var subQ0=sQuery(id+"F0.wireOp",EDGE,"E15");var subQ1=sQuery(id+"F0.wireOp",EDGE,"E9");var subQ2=makeQuery(id+"F0.imprint","INTERSECT",VERTEX,{"derivedFrom":[subQ1,subQ0]});Q64=makeQuery(id+"F0.imprint","IMPRINT",FACE,{"disambiguationData":[TD([[makeQuery(id+"F0.imprint","IMPRINT",EDGE,{"disambiguationData":[TD([[subQ2,-1.0]])],"derivedFrom":subQ1}),1.0]])]});}
            var Q65;
            {var subQ0=sQuery(id+"F0.wireOp",EDGE,"E12");var subQ1=sQuery(id+"F0.wireOp",EDGE,"E9");var subQ2=makeQuery(id+"F0.imprint","INTERSECT",VERTEX,{"derivedFrom":[subQ1,subQ0]});Q65=makeQuery(id+"F0.imprint","IMPRINT",FACE,{"disambiguationData":[TD([[makeQuery(id+"F0.imprint","IMPRINT",EDGE,{"disambiguationData":[TD([[subQ2,-1.0]])],"derivedFrom":subQ1}),1.0]])]});}
            var Q66;
            {var subQ0=sQuery(id+"F0.wireOp",EDGE,"E15");var subQ1=sQuery(id+"F0.wireOp",EDGE,"E3");var subQ2=makeQuery(id+"F0.imprint","INTERSECT",VERTEX,{"derivedFrom":[subQ1,subQ0]});Q66=makeQuery(id+"F0.imprint","IMPRINT",FACE,{"disambiguationData":[TD([[makeQuery(id+"F0.imprint","IMPRINT",EDGE,{"disambiguationData":[TD([[subQ2,-1.0]])],"derivedFrom":subQ1}),1.0]])]});}
            var Q67;
            {var subQ0=sQuery(id+"F0.wireOp",EDGE,"E12");var subQ1=sQuery(id+"F0.wireOp",EDGE,"E4");var subQ2=makeQuery(id+"F0.imprint","INTERSECT",VERTEX,{"derivedFrom":[subQ1,subQ0]});Q67=makeQuery(id+"F0.imprint","IMPRINT",FACE,{"disambiguationData":[TD([[makeQuery(id+"F0.imprint","IMPRINT",EDGE,{"disambiguationData":[TD([[subQ2,-1.0]])],"derivedFrom":subQ1}),1.0]])]});}
            var Q68;
            {var subQ0=sQuery(id+"F0.wireOp",EDGE,"E12");var subQ1=sQuery(id+"F0.wireOp",EDGE,"E3");var subQ2=makeQuery(id+"F0.imprint","INTERSECT",VERTEX,{"derivedFrom":[subQ1,subQ0]});Q68=makeQuery(id+"F0.imprint","IMPRINT",FACE,{"disambiguationData":[TD([[makeQuery(id+"F0.imprint","IMPRINT",EDGE,{"disambiguationData":[TD([[subQ2,-1.0]])],"derivedFrom":subQ1}),1.0]])]});}
            var Q69;
            {var subQ0=sQuery(id+"F0.wireOp",EDGE,"E3");var subQ1=sQuery(id+"F0.wireOp",EDGE,"E0");var subQ2=makeQuery(id+"F0.imprint","INTERSECT",VERTEX,{"disambiguationData":[OD(0.0)],"derivedFrom":[subQ1,subQ0]});Q69=makeQuery(id+"F0.imprint","IMPRINT",FACE,{"disambiguationData":[TD([[makeQuery(id+"F0.imprint","IMPRINT",EDGE,{"disambiguationData":[TD([[subQ2,-1.0]])],"derivedFrom":subQ1}),1.0]])]});}
            var Q70;
            {var subQ0=sQuery(id+"F0.wireOp",EDGE,"E3");var subQ1=sQuery(id+"F0.wireOp",EDGE,"E0");var subQ2=makeQuery(id+"F0.imprint","INTERSECT",VERTEX,{"disambiguationData":[OD(0.0)],"derivedFrom":[subQ1,subQ0]});Q70=makeQuery(id+"F0.imprint","IMPRINT",FACE,{"disambiguationData":[TD([[makeQuery(id+"F0.imprint","IMPRINT",EDGE,{"disambiguationData":[TD([[subQ2,-1.0]])],"derivedFrom":subQ1}),-1.0]])]});}
            var Q71;
            {var subQ0=sQuery(id+"F0.wireOp",EDGE,"E12");var subQ1=sQuery(id+"F0.wireOp",EDGE,"E0");var subQ2=makeQuery(id+"F0.imprint","INTERSECT",VERTEX,{"disambiguationData":[OD(0.0)],"derivedFrom":[subQ1,subQ0]});Q71=makeQuery(id+"F0.imprint","IMPRINT",FACE,{"disambiguationData":[TD([[makeQuery(id+"F0.imprint","IMPRINT",EDGE,{"disambiguationData":[TD([[subQ2,-1.0]])],"derivedFrom":subQ1}),-1.0]])]});}
            var Q72;
            {var subQ0=sQuery(id+"F0.wireOp",EDGE,"E12");var subQ1=sQuery(id+"F0.wireOp",EDGE,"E0");var subQ2=makeQuery(id+"F0.imprint","INTERSECT",VERTEX,{"disambiguationData":[OD(0.0)],"derivedFrom":[subQ1,subQ0]});Q72=makeQuery(id+"F0.imprint","IMPRINT",FACE,{"disambiguationData":[TD([[makeQuery(id+"F0.imprint","IMPRINT",EDGE,{"disambiguationData":[TD([[subQ2,-1.0]])],"derivedFrom":subQ1}),1.0]])]});}
            var Q73;
            {var subQ0=sQuery(id+"F0.wireOp",EDGE,"E16");var subQ1=sQuery(id+"F0.wireOp",EDGE,"E0");var subQ2=makeQuery(id+"F0.imprint","INTERSECT",VERTEX,{"disambiguationData":[OD(0.0)],"derivedFrom":[subQ1,subQ0]});Q73=makeQuery(id+"F0.imprint","IMPRINT",FACE,{"disambiguationData":[TD([[makeQuery(id+"F0.imprint","IMPRINT",EDGE,{"disambiguationData":[TD([[subQ2,-1.0]])],"derivedFrom":subQ1}),1.0]])]});}
            var Q74;
            {var subQ0=sQuery(id+"F0.wireOp",EDGE,"E16");var subQ1=sQuery(id+"F0.wireOp",EDGE,"E3");var subQ2=makeQuery(id+"F0.imprint","INTERSECT",VERTEX,{"derivedFrom":[subQ1,subQ0]});Q74=makeQuery(id+"F0.imprint","IMPRINT",FACE,{"disambiguationData":[TD([[makeQuery(id+"F0.imprint","IMPRINT",EDGE,{"disambiguationData":[TD([[subQ2,-1.0]])],"derivedFrom":subQ1}),1.0]])]});}
            var Q75;
            {var subQ0=sQuery(id+"F0.wireOp",EDGE,"E16");var subQ1=sQuery(id+"F0.wireOp",EDGE,"E4");var subQ2=makeQuery(id+"F0.imprint","INTERSECT",VERTEX,{"derivedFrom":[subQ1,subQ0]});Q75=makeQuery(id+"F0.imprint","IMPRINT",FACE,{"disambiguationData":[TD([[makeQuery(id+"F0.imprint","IMPRINT",EDGE,{"disambiguationData":[TD([[subQ2,-1.0]])],"derivedFrom":subQ1}),1.0]])]});}
            var Q76;
            {var subQ0=sQuery(id+"F0.wireOp",EDGE,"E21");var subQ1=sQuery(id+"F0.wireOp",EDGE,"E3");var subQ2=makeQuery(id+"F0.imprint","INTERSECT",VERTEX,{"derivedFrom":[subQ1,subQ0]});Q76=makeQuery(id+"F0.imprint","IMPRINT",FACE,{"disambiguationData":[TD([[makeQuery(id+"F0.imprint","IMPRINT",EDGE,{"disambiguationData":[TD([[subQ2,-1.0]])],"derivedFrom":subQ1}),1.0]])]});}
            var Q77;
            {var subQ0=sQuery(id+"F0.wireOp",EDGE,"E16");var subQ1=sQuery(id+"F0.wireOp",EDGE,"E9");var subQ2=makeQuery(id+"F0.imprint","INTERSECT",VERTEX,{"derivedFrom":[subQ1,subQ0]});Q77=makeQuery(id+"F0.imprint","IMPRINT",FACE,{"disambiguationData":[TD([[makeQuery(id+"F0.imprint","IMPRINT",EDGE,{"disambiguationData":[TD([[subQ2,-1.0]])],"derivedFrom":subQ1}),1.0]])]});}
            var Q78;
            {var subQ0=sQuery(id+"F0.wireOp",EDGE,"E21");var subQ1=sQuery(id+"F0.wireOp",EDGE,"E9");var subQ2=makeQuery(id+"F0.imprint","INTERSECT",VERTEX,{"derivedFrom":[subQ1,subQ0]});Q78=makeQuery(id+"F0.imprint","IMPRINT",FACE,{"disambiguationData":[TD([[makeQuery(id+"F0.imprint","IMPRINT",EDGE,{"disambiguationData":[TD([[subQ2,-1.0]])],"derivedFrom":subQ1}),-1.0]])]});}
            var Q79;
            {var subQ0=sQuery(id+"F0.wireOp",EDGE,"E21");var subQ1=sQuery(id+"F0.wireOp",EDGE,"E9");var subQ2=makeQuery(id+"F0.imprint","INTERSECT",VERTEX,{"derivedFrom":[subQ1,subQ0]});Q79=makeQuery(id+"F0.imprint","IMPRINT",FACE,{"disambiguationData":[TD([[makeQuery(id+"F0.imprint","IMPRINT",EDGE,{"disambiguationData":[TD([[subQ2,-1.0]])],"derivedFrom":subQ1}),1.0]])]});}
            var Q80;
            {var subQ0=sQuery(id+"F0.wireOp",EDGE,"E22");var subQ1=sQuery(id+"F0.wireOp",EDGE,"E4");var subQ2=makeQuery(id+"F0.imprint","INTERSECT",VERTEX,{"derivedFrom":[subQ1,subQ0]});Q80=makeQuery(id+"F0.imprint","IMPRINT",FACE,{"disambiguationData":[TD([[makeQuery(id+"F0.imprint","IMPRINT",EDGE,{"disambiguationData":[TD([[subQ2,-1.0]])],"derivedFrom":subQ1}),1.0]])]});}
            var Q81;
            {var subQ0=sQuery(id+"F0.wireOp",EDGE,"E22");var subQ1=sQuery(id+"F0.wireOp",EDGE,"E3");var subQ2=makeQuery(id+"F0.imprint","INTERSECT",VERTEX,{"derivedFrom":[subQ1,subQ0]});Q81=makeQuery(id+"F0.imprint","IMPRINT",FACE,{"disambiguationData":[TD([[makeQuery(id+"F0.imprint","IMPRINT",EDGE,{"disambiguationData":[TD([[subQ2,-1.0]])],"derivedFrom":subQ1}),1.0]])]});}
            var Q82;
            {var subQ0=sQuery(id+"F0.wireOp",EDGE,"E16");var subQ1=sQuery(id+"F0.wireOp",EDGE,"E0");var subQ2=makeQuery(id+"F0.imprint","INTERSECT",VERTEX,{"disambiguationData":[OD(0.0)],"derivedFrom":[subQ1,subQ0]});Q82=makeQuery(id+"F0.imprint","IMPRINT",FACE,{"disambiguationData":[TD([[makeQuery(id+"F0.imprint","IMPRINT",EDGE,{"disambiguationData":[TD([[subQ2,-1.0]])],"derivedFrom":subQ1}),-1.0]])]});}
            var Q83;
            {var subQ0=sQuery(id+"F0.wireOp",EDGE,"E21");var subQ1=sQuery(id+"F0.wireOp",EDGE,"E0");var subQ2=makeQuery(id+"F0.imprint","INTERSECT",VERTEX,{"disambiguationData":[OD(0.0)],"derivedFrom":[subQ1,subQ0]});Q83=makeQuery(id+"F0.imprint","IMPRINT",FACE,{"disambiguationData":[TD([[makeQuery(id+"F0.imprint","IMPRINT",EDGE,{"disambiguationData":[TD([[subQ2,1.0]])],"derivedFrom":subQ1}),-1.0]])]});}
            var Q84;
            {var subQ0=sQuery(id+"F0.wireOp",EDGE,"E2.right");var subQ1=sQuery(id+"F0.wireOp",EDGE,"E0");var subQ2=makeQuery(id+"F0.imprint","INTERSECT",VERTEX,{"derivedFrom":[subQ1,subQ0]});Q84=makeQuery(id+"F0.imprint","IMPRINT",FACE,{"disambiguationData":[TD([[makeQuery(id+"F0.imprint","IMPRINT",EDGE,{"disambiguationData":[TD([[subQ2,1.0]])],"derivedFrom":subQ1}),-1.0]])]});}
            var Q85;
            {var subQ0=sQuery(id+"F0.wireOp",EDGE,"E21");var subQ1=sQuery(id+"F0.wireOp",EDGE,"E0");var subQ2=makeQuery(id+"F0.imprint","INTERSECT",VERTEX,{"disambiguationData":[OD(0.0)],"derivedFrom":[subQ1,subQ0]});Q85=makeQuery(id+"F0.imprint","IMPRINT",FACE,{"disambiguationData":[TD([[makeQuery(id+"F0.imprint","IMPRINT",EDGE,{"disambiguationData":[TD([[subQ2,1.0]])],"derivedFrom":subQ1}),1.0]])]});}
            var Q86;
            {var subQ0=sQuery(id+"F0.wireOp",EDGE,"E17");var subQ1=sQuery(id+"F0.wireOp",EDGE,"E9");var subQ2=makeQuery(id+"F0.imprint","INTERSECT",VERTEX,{"derivedFrom":[subQ1,subQ0]});Q86=makeQuery(id+"F0.imprint","IMPRINT",FACE,{"disambiguationData":[TD([[makeQuery(id+"F0.imprint","IMPRINT",EDGE,{"disambiguationData":[TD([[subQ2,-1.0]])],"derivedFrom":subQ1}),-1.0]])]});}
            var Q87;
            {var subQ0=sQuery(id+"F0.wireOp",EDGE,"E17");var subQ1=sQuery(id+"F0.wireOp",EDGE,"E9");var subQ2=makeQuery(id+"F0.imprint","INTERSECT",VERTEX,{"derivedFrom":[subQ1,subQ0]});Q87=makeQuery(id+"F0.imprint","IMPRINT",FACE,{"disambiguationData":[TD([[makeQuery(id+"F0.imprint","IMPRINT",EDGE,{"disambiguationData":[TD([[subQ2,-1.0]])],"derivedFrom":subQ1}),1.0]])]});}
            var Q88;
            {var subQ0=sQuery(id+"F0.wireOp",EDGE,"E22");var subQ1=sQuery(id+"F0.wireOp",EDGE,"E9");var subQ2=makeQuery(id+"F0.imprint","INTERSECT",VERTEX,{"derivedFrom":[subQ1,subQ0]});Q88=makeQuery(id+"F0.imprint","IMPRINT",FACE,{"disambiguationData":[TD([[makeQuery(id+"F0.imprint","IMPRINT",EDGE,{"disambiguationData":[TD([[subQ2,-1.0]])],"derivedFrom":subQ1}),1.0]])]});}
            var Q89;
            {var subQ0=sQuery(id+"F0.wireOp",EDGE,"E18");var subQ1=sQuery(id+"F0.wireOp",EDGE,"E4");var subQ2=makeQuery(id+"F0.imprint","INTERSECT",VERTEX,{"derivedFrom":[subQ1,subQ0]});Q89=makeQuery(id+"F0.imprint","IMPRINT",FACE,{"disambiguationData":[TD([[makeQuery(id+"F0.imprint","IMPRINT",EDGE,{"disambiguationData":[TD([[subQ2,-1.0]])],"derivedFrom":subQ1}),1.0]])]});}
            var Q90;
            {var subQ0=sQuery(id+"F0.wireOp",EDGE,"E18");var subQ1=sQuery(id+"F0.wireOp",EDGE,"E9");var subQ2=makeQuery(id+"F0.imprint","INTERSECT",VERTEX,{"derivedFrom":[subQ1,subQ0]});Q90=makeQuery(id+"F0.imprint","IMPRINT",FACE,{"disambiguationData":[TD([[makeQuery(id+"F0.imprint","IMPRINT",EDGE,{"disambiguationData":[TD([[subQ2,-1.0]])],"derivedFrom":subQ1}),1.0]])]});}
            var Q91;
            {var subQ0=sQuery(id+"F0.wireOp",EDGE,"E14");var subQ1=sQuery(id+"F0.wireOp",EDGE,"E3");var subQ2=makeQuery(id+"F0.imprint","INTERSECT",VERTEX,{"derivedFrom":[subQ1,subQ0]});Q91=makeQuery(id+"F0.imprint","IMPRINT",FACE,{"disambiguationData":[TD([[makeQuery(id+"F0.imprint","IMPRINT",EDGE,{"disambiguationData":[TD([[subQ2,-1.0]])],"derivedFrom":subQ1}),1.0]])]});}
            var Q92;
            {var subQ0=sQuery(id+"F0.wireOp",EDGE,"E18");var subQ1=sQuery(id+"F0.wireOp",EDGE,"E3");var subQ2=makeQuery(id+"F0.imprint","INTERSECT",VERTEX,{"derivedFrom":[subQ1,subQ0]});Q92=makeQuery(id+"F0.imprint","IMPRINT",FACE,{"disambiguationData":[TD([[makeQuery(id+"F0.imprint","IMPRINT",EDGE,{"disambiguationData":[TD([[subQ2,-1.0]])],"derivedFrom":subQ1}),1.0]])]});}
            var Q93;
            {var subQ0=sQuery(id+"F0.wireOp",EDGE,"E17");var subQ1=sQuery(id+"F0.wireOp",EDGE,"E3");var subQ2=makeQuery(id+"F0.imprint","INTERSECT",VERTEX,{"derivedFrom":[subQ1,subQ0]});Q93=makeQuery(id+"F0.imprint","IMPRINT",FACE,{"disambiguationData":[TD([[makeQuery(id+"F0.imprint","IMPRINT",EDGE,{"disambiguationData":[TD([[subQ2,-1.0]])],"derivedFrom":subQ1}),1.0]])]});}
            var Q94;
            {var subQ0=sQuery(id+"F0.wireOp",EDGE,"E18");var subQ1=sQuery(id+"F0.wireOp",EDGE,"E0");var subQ2=makeQuery(id+"F0.imprint","INTERSECT",VERTEX,{"disambiguationData":[OD(1.0)],"derivedFrom":[subQ1,subQ0]});Q94=makeQuery(id+"F0.imprint","IMPRINT",FACE,{"disambiguationData":[TD([[makeQuery(id+"F0.imprint","IMPRINT",EDGE,{"disambiguationData":[TD([[subQ2,-1.0]])],"derivedFrom":subQ1}),1.0]])]});}
            var Q95;
            {var subQ0=sQuery(id+"F0.wireOp",EDGE,"E18");var subQ1=sQuery(id+"F0.wireOp",EDGE,"E0");var subQ2=makeQuery(id+"F0.imprint","INTERSECT",VERTEX,{"disambiguationData":[OD(1.0)],"derivedFrom":[subQ1,subQ0]});Q95=makeQuery(id+"F0.imprint","IMPRINT",FACE,{"disambiguationData":[TD([[makeQuery(id+"F0.imprint","IMPRINT",EDGE,{"disambiguationData":[TD([[subQ2,-1.0]])],"derivedFrom":subQ1}),-1.0]])]});}
            var Q96;
            {var subQ0=sQuery(id+"F0.wireOp",EDGE,"E13");var subQ1=sQuery(id+"F0.wireOp",EDGE,"E0");var subQ2=makeQuery(id+"F0.imprint","INTERSECT",VERTEX,{"disambiguationData":[OD(1.0)],"derivedFrom":[subQ1,subQ0]});Q96=makeQuery(id+"F0.imprint","IMPRINT",FACE,{"disambiguationData":[TD([[makeQuery(id+"F0.imprint","IMPRINT",EDGE,{"disambiguationData":[TD([[subQ2,-1.0]])],"derivedFrom":subQ1}),-1.0]])]});}
            var Q97;
            {var subQ0=sQuery(id+"F0.wireOp",EDGE,"E13");var subQ1=sQuery(id+"F0.wireOp",EDGE,"E0");var subQ2=makeQuery(id+"F0.imprint","INTERSECT",VERTEX,{"disambiguationData":[OD(1.0)],"derivedFrom":[subQ1,subQ0]});Q97=makeQuery(id+"F0.imprint","IMPRINT",FACE,{"disambiguationData":[TD([[makeQuery(id+"F0.imprint","IMPRINT",EDGE,{"disambiguationData":[TD([[subQ2,-1.0]])],"derivedFrom":subQ1}),1.0]])]});}
            var Q98;
            {var subQ0=sQuery(id+"F0.wireOp",EDGE,"E13");var subQ1=sQuery(id+"F0.wireOp",EDGE,"E3");var subQ2=makeQuery(id+"F0.imprint","INTERSECT",VERTEX,{"derivedFrom":[subQ1,subQ0]});Q98=makeQuery(id+"F0.imprint","IMPRINT",FACE,{"disambiguationData":[TD([[makeQuery(id+"F0.imprint","IMPRINT",EDGE,{"disambiguationData":[TD([[subQ2,-1.0]])],"derivedFrom":subQ1}),1.0]])]});}
            var Q99;
            {var subQ0=sQuery(id+"F0.wireOp",EDGE,"E4");var subQ1=sQuery(id+"F0.wireOp",EDGE,"E0");var subQ2=makeQuery(id+"F0.imprint","INTERSECT",VERTEX,{"disambiguationData":[OD(1.0)],"derivedFrom":[subQ1,subQ0]});Q99=makeQuery(id+"F0.imprint","IMPRINT",FACE,{"disambiguationData":[TD([[makeQuery(id+"F0.imprint","IMPRINT",EDGE,{"disambiguationData":[TD([[subQ2,-1.0]])],"derivedFrom":subQ1}),1.0]])]});}
            var Q100;
            {var subQ0=sQuery(id+"F0.wireOp",EDGE,"E4");var subQ1=sQuery(id+"F0.wireOp",EDGE,"E0");var subQ2=makeQuery(id+"F0.imprint","INTERSECT",VERTEX,{"disambiguationData":[OD(1.0)],"derivedFrom":[subQ1,subQ0]});Q100=makeQuery(id+"F0.imprint","IMPRINT",FACE,{"disambiguationData":[TD([[makeQuery(id+"F0.imprint","IMPRINT",EDGE,{"disambiguationData":[TD([[subQ2,-1.0]])],"derivedFrom":subQ1}),-1.0]])]});}
            var Q101;
            {var subQ0=sQuery(id+"F0.wireOp",EDGE,"E9");var subQ1=sQuery(id+"F0.wireOp",EDGE,"E0");var subQ2=makeQuery(id+"F0.imprint","INTERSECT",VERTEX,{"disambiguationData":[OD(1.0)],"derivedFrom":[subQ1,subQ0]});Q101=makeQuery(id+"F0.imprint","IMPRINT",FACE,{"disambiguationData":[TD([[makeQuery(id+"F0.imprint","IMPRINT",EDGE,{"disambiguationData":[TD([[subQ2,-1.0]])],"derivedFrom":subQ1}),1.0]])]});}
            var Q102;
            {var subQ0=sQuery(id+"F0.wireOp",EDGE,"E14");var subQ1=sQuery(id+"F0.wireOp",EDGE,"E9");var subQ2=makeQuery(id+"F0.imprint","INTERSECT",VERTEX,{"derivedFrom":[subQ1,subQ0]});Q102=makeQuery(id+"F0.imprint","IMPRINT",FACE,{"disambiguationData":[TD([[makeQuery(id+"F0.imprint","IMPRINT",EDGE,{"disambiguationData":[TD([[subQ2,-1.0]])],"derivedFrom":subQ1}),1.0]])]});}
            var Q103;
            {var subQ0=sQuery(id+"F0.wireOp",EDGE,"E13");var subQ1=sQuery(id+"F0.wireOp",EDGE,"E4");var subQ2=makeQuery(id+"F0.imprint","INTERSECT",VERTEX,{"derivedFrom":[subQ1,subQ0]});Q103=makeQuery(id+"F0.imprint","IMPRINT",FACE,{"disambiguationData":[TD([[makeQuery(id+"F0.imprint","IMPRINT",EDGE,{"disambiguationData":[TD([[subQ2,-1.0]])],"derivedFrom":subQ1}),1.0]])]});}
            var Q104;
            {var subQ0=sQuery(id+"F0.wireOp",EDGE,"E14");var subQ1=sQuery(id+"F0.wireOp",EDGE,"E9");var subQ2=makeQuery(id+"F0.imprint","INTERSECT",VERTEX,{"derivedFrom":[subQ1,subQ0]});Q104=makeQuery(id+"F0.imprint","IMPRINT",FACE,{"disambiguationData":[TD([[makeQuery(id+"F0.imprint","IMPRINT",EDGE,{"disambiguationData":[TD([[subQ2,-1.0]])],"derivedFrom":subQ1}),-1.0]])]});}
            var Q105;
            {var subQ0=sQuery(id+"F0.wireOp",EDGE,"E19");var subQ1=sQuery(id+"F0.wireOp",EDGE,"E0");var subQ2=makeQuery(id+"F0.imprint","INTERSECT",VERTEX,{"disambiguationData":[OD(1.0)],"derivedFrom":[subQ1,subQ0]});Q105=makeQuery(id+"F0.imprint","IMPRINT",FACE,{"disambiguationData":[TD([[makeQuery(id+"F0.imprint","IMPRINT",EDGE,{"disambiguationData":[TD([[subQ2,-1.0]])],"derivedFrom":subQ1}),1.0]])]});}
            var Q106;
            {var subQ0=sQuery(id+"F0.wireOp",EDGE,"E6");var subQ1=sQuery(id+"F0.wireOp",EDGE,"E0");var subQ2=makeQuery(id+"F0.imprint","INTERSECT",VERTEX,{"disambiguationData":[OD(1.0)],"derivedFrom":[subQ1,subQ0]});Q106=makeQuery(id+"F0.imprint","IMPRINT",FACE,{"disambiguationData":[TD([[makeQuery(id+"F0.imprint","IMPRINT",EDGE,{"disambiguationData":[TD([[subQ2,-1.0]])],"derivedFrom":subQ1}),-1.0]])]});}
            var Q107;
            {var subQ0=sQuery(id+"F0.wireOp",EDGE,"E9");var subQ1=sQuery(id+"F0.wireOp",EDGE,"E0");var subQ2=makeQuery(id+"F0.imprint","INTERSECT",VERTEX,{"disambiguationData":[OD(1.0)],"derivedFrom":[subQ1,subQ0]});Q107=makeQuery(id+"F0.imprint","IMPRINT",FACE,{"disambiguationData":[TD([[makeQuery(id+"F0.imprint","IMPRINT",EDGE,{"disambiguationData":[TD([[subQ2,-1.0]])],"derivedFrom":subQ1}),-1.0]])]});}
            var Q108;
            {var subQ0=sQuery(id+"F0.wireOp",EDGE,"E2.top");var subQ1=sQuery(id+"F0.wireOp",EDGE,"E0");var subQ2=makeQuery(id+"F0.imprint","INTERSECT",VERTEX,{"derivedFrom":[subQ1,subQ0]});Q108=makeQuery(id+"F0.imprint","IMPRINT",FACE,{"disambiguationData":[TD([[makeQuery(id+"F0.imprint","IMPRINT",EDGE,{"disambiguationData":[TD([[subQ2,-1.0]])],"derivedFrom":subQ1}),-1.0]])]});}
            var Q109;
            {var subQ0=sQuery(id+"F0.wireOp",EDGE,"E19");var subQ1=sQuery(id+"F0.wireOp",EDGE,"E0");var subQ2=makeQuery(id+"F0.imprint","INTERSECT",VERTEX,{"disambiguationData":[OD(1.0)],"derivedFrom":[subQ1,subQ0]});Q109=makeQuery(id+"F0.imprint","IMPRINT",FACE,{"disambiguationData":[TD([[makeQuery(id+"F0.imprint","IMPRINT",EDGE,{"disambiguationData":[TD([[subQ2,-1.0]])],"derivedFrom":subQ1}),-1.0]])]});}
            extrude(context, id + "F1", {"entities" : qUnion([Q0, Q1, Q2, Q3, Q4, Q5, Q6, Q7, Q8, Q9, Q10, Q11, Q12, Q13, Q14, Q15, Q16, Q17, Q18, Q19, Q20, Q21, Q22, Q23, Q24, Q25, Q26, Q27, Q28, Q29, Q30, Q31, Q32, Q33, Q34, Q35, Q36, Q37, Q38, Q39, Q40, Q41, Q42, Q43, Q44, Q45, Q46, Q47, Q48, Q49, Q50, Q51, Q52, Q53, Q54, Q55, Q56, Q57, Q58, Q59, Q60, Q61, Q62, Q63, Q64, Q65, Q66, Q67, Q68, Q69, Q70, Q71, Q72, Q73, Q74, Q75, Q76, Q77, Q78, Q79, Q80, Q81, Q82, Q83, Q84, Q85, Q86, Q87, Q88, Q89, Q90, Q91, Q92, Q93, Q94, Q95, Q96, Q97, Q98, Q99, Q100, Q101, Q102, Q103, Q104, Q105, Q106, Q107, Q108, Q109]), "depth" : 206.8 * mm});
        }
    });
